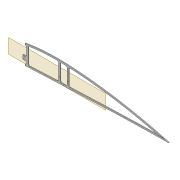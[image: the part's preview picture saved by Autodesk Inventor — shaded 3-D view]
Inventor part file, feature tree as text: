
AUTODESK INVENTOR PART (.ipt)
format: ipt  version: 2022 (Build 260153000, 153)  size: 573,440 bytes
history: native  units: mm
features: sketch x9, projected_geometry x9, extrude x8, fillet x2, shell x1, plane x1, chamfer x1
ambient origin geometry x8: Origin, YZ Plane, XZ Plane, XY Plane, X Axis, Y Axis, Z Axis, Center Point
bodies: Solid1 (feature_tree)
feature tree (31):
  extrude  "Extrusion1"  Depth=4.0mm
  shell  "Shell1"  Thickness=2.0mm
  extrude  "Extrusion8"  Depth=5.9mm
  extrude  "Extrusion3"  Depth=10.0mm TaperAngle=0.0deg
  extrude  "Extrusion4"  Depth=2.0mm
  fillet  "Fillet1"  Radius=5.0mm
  sketch  "Sketch10"  dims[d22=2.0mm d23=0.0mm d31=2.0mm d32=5.0mm]
  extrude  "Extrusion5"  Depth=2.5mm
  plane  "Work Plane2"
  extrude  "Extrusion9"  Depth=1.6mm
  fillet  "Fillet2"  Radius=2.5mm
  extrude  "Extrusion10"  Depth=6.0mm
  chamfer  "Chamfer1"  Distance=2.0mm
  extrude  "Extrusion12"  Depth=12.0mm
  sketch  "Sketch29"  dims[d66=3.0mm d67=12.0mm]
  sketch  "Sketch30"  dims[d68=5.0mm d69=10.0mm d70=12.0mm d71=3.05mm d72=10.0mm d73=0.0mm d74=2.0mm d75=100.0mm d76=20.0mm d77=0.5mm d78=10.0mm d79=0.0mm d82=3.0mm d83=2.0mm d84=45.0deg d85=1.0mm d86=1.0mm d87=1.0mm d88=1.0mm d89=1.0mm d90=1.0mm d91=10.0mm d92=0.0mm]
  sketch  "Sketch3"  dims[d0=2.0mm d1=0.0mm d2=4.0mm d7=2.0mm]
  sketch  "Sketch8"  dims[d8=2.0mm d9=5.9mm]
  sketch  "Sketch9"  dims[d13=10.0mm d14=0.0mm d16=10.0mm d17=0.0mm]
  projected_geometry  "Projected Loop4"
  projected_geometry  "Projected Loop10"
  sketch  "Sketch24"  dims[d34=1.6mm d35=2.5mm]
  projected_geometry  "Projected Loop11"
  projected_geometry  "Projected Loop12"
  projected_geometry  "Projected Loop13"
  sketch  "Sketch26"  dims[d37=5.0mm d38=1.6mm d40=2.5mm]
  projected_geometry  "Projected Loop14"
  sketch  "Sketch28"  dims[d62=80.0mm d63=6.0mm d64=2.0mm d65=0.0mm]
  projected_geometry  "Project Cut Edges1"
  projected_geometry  "Project Cut Edges2"
  projected_geometry  "Project Cut Edges3"
